# Revit family: Plate_System_Water_Coolers-Zurn-Industries-Z1224
name_source: partatom
category: Plumbing Fixtures
units: mm (PartAtom-declared; Revit-internal decimal feet)

## family parameters
Cut with Voids When Loaded = No
Host = Face
Maintain Annotation Orientation = No
OmniClass Number = 23.45.05.21.11.14
OmniClass Title = Chemical/Biological Sanitary Disposal Units
Part Type = Normal
Room Calculation Point = No
Round Connector Dimension = Use Diameter
Shared = No

## types (38) — shared parameters
A Dimension = 18.25 "
Approx.wt.lbs = 28
Assembly Code = D2030100
CW Connection = No
Curve inner radius = 1.5 "
Default Elevation = 25 "
Description = Plate Type System Lavatory With Back
HW Connection = No
Hardware = Steel - Zurn - Zinc Coated
Manufacturer = Zurn Water, LLC
Manufacturer Brand = Zurn
Model = Z1224
Modified Date = 10/31/2025
Product Data URL = https://www.bimobject.com
Product Documentation Link = https://files.zurn.com
Product Installation Sheet URL = https://files.zurn.com
Product Page URL = https://www.zurn.com
System with Universal Plate = Iron - Zurn - Cast - Painted - Blue
URL = www.zurn.com
Vent Connection = No
WFU = 1
Waste Connection = Yes
Width = 2.5 "
zero-valued in all types: CWFU, HWFU

## per-type parameters (varying)
| type | B Dimension | D Dimension | D' Dimension (Zurn) | Double Installtion Holes | E Dimension | E' Dimension | H Dimension | Single Installation Holes | Type Comments |
| American Standard®-Allbrook™ (6541.132) | 31.75 " | 12 " | 1.188 " | No | 0.594 " | 0.594 " | 36 " | Yes | American Standard®-Allbrook™ (6541.132) |
| Zurn-Small Waterless (Z5796) | 30.875 " | 12 " | 1 " | No | 0.5 " | 0.5 " | 36 " | Yes | Zurn-Small Waterless (Z5796) |
| Zurn-Urinal (Z5740) | 31.75 " | 12 " | 1 " | No | 0.5 " | 0.5 " | 36 " | Yes | Zurn-Urinal (Z5740) |
| Zurn-Small Pint (Z5738) | 32 " | 12 " | 1 " | No | 0.5 " | 0.5 " | 36 " | Yes | Zurn-Small Pint (Z5738) |
| Kohler®-Bardon™ (K-4960) | 41.25 " | 12 " | 1 " | Yes | 0.5 " | 0.5 " | 48 " | No | Kohler®-Bardon™ (K-4960) |
| Kohler®-Bardon™ (K-4904-ET) | 41.25 " | 12 " | 1 " | Yes | 0.5 " | 0.5 " | 48 " | No | Kohler®-Bardon™ (K-4904-ET) |
| American Standard®-Trimbrook™ (6561-017) | 38.375 " | 11 " | 1 " | Yes | 0.594 " | 0.5 " | 42 " | No | American Standard®-Trimbrook™ (6561.017) |
| American Standard®-Washbrook™ (6590-525) | 39.5 " | 13.5 " | 1 " | Yes | 0.594 " | 0.5 " | 42 " | No | American Standard®-Washbrook™ (6590.525) |
| American Standard®-Washbrook™ (6590-125) | 39.5 " | 13.5 " | 1 " | Yes | 0.594 " | 0.5 " | 42 " | No | American Standard®-Washbrook™ (6590.125) |
| American Standard®-Washbrook™ (6515-125) | 39.5 " | 13.5 " | 1 " | Yes | 0.594 " | 0.5 " | 42 " | No | American Standard®-Washbrook™ (6515.125) |
| American Standard®-Washbrook™ (6506-011) | 39.75 " | 13.5 " | 1 " | Yes | 0.594 " | 0.5 " | 42 " | No | American Standard®-Washbrook™ (6506.011) |
| American Standard®-Washbrook™ (6501-010) | 39.75 " | 13.5 " | 1 " | Yes | 0.594 " | 0.5 " | 42 " | No | American Standard®-Washbrook™ (6501.010) |
| Eljer®-Signature™ (161-2095) | 36.5 " | 11 " | 1 " | Yes | 0.5 " | 0.5 " | 42 " | No | Eljer®-Signature™ (161-2095) |
| Eljer®-Signature™ (161-2090) | 36.5 " | 11 " | 1 " | Yes | 0.5 " | 0.5 " | 42 " | No | Eljer®-Signature™ (161-2090) |
| Eljer®-Bedfordshire™ (161-1190) | 32.125 " | 6 " | 1 " | Yes | 0.5 " | 0.5 " | 36 " | No | Eljer®-Bedfordshire™ (161-1190) |
| Eljer®-Dover™ (161-1150) | 33.125 " | 6 " | 1 " | Yes | 0.5 " | 0.5 " | 36 " | No | Eljer®-Dover™ (161-1150) |
| Eljer®-Savon™ (161-1095) | 36.5 " | 11 " | 1 " | Yes | 0.5 " | 0.5 " | 42 " | No | Eljer®-Savon™ (161-1095) |
| Eljer®-Savon™ (161-1090) | 36.5 " | 11 " | 1 " | Yes | 0.5 " | 0.5 " | 42 " | No | Eljer®-Savon™ (161-1090) |
| Eljer®-Correcto™ (161-1075) | 40.125 " | 12 " | 1 " | Yes | 0.5 " | 0.5 " | 48 " | No | Eljer®-Correcto™ (161-1075) |
| Eljer®-Correcto™ (161-1060) | 40.125 " | 12 " | 1 " | Yes | 0.5 " | 0.5 " | 48 " | No | Eljer®-Correcto™ (161-1060) |
| Eljer®-Correcto™ (161-1045) | 40.125 " | 12 " | 1 " | Yes | 0.5 " | 0.5 " | 48 " | No | Eljer®-Correcto™ (161-1045) |
| Zurn-Urinal (Z5730) | 31.75 " | 12 " | 1 " | No | 0.5 " | 0.5 " | 36 " | Yes | Zurn-Urinal (Z5730) |
| Eljer®-Correcto™ (161-1030) | 40.125 " | 12 " | 1 " | Yes | 0.5 " | 0.5 " | 48 " | No | Eljer®-Correcto™ (161-1030) |
| American Standard®-Pintbrook™ (6002-001) | 33.375 " | 6 " | 1 " | Yes | 0.594 " | 0.5 " | 36 " | No | American Standard®-Pintbrook™ (6002.001) |
| Eljer®-Correcto™ (161-1035) | 40.125 " | 12 " | 1 " | Yes | 0.5 " | 0.5 " | 48 " | No | Eljer®-Correcto™ (161-1035) |
| Eljer®-Correcto™ (161-1050) | 40.125 " | 12 " | 1 " | Yes | 0.5 " | 0.5 " | 48 " | No | Eljer®-Correcto™ (161-1050) |
| Eljer®-Correcto™ (161-1065) | 40.125 " | 12 " | 1 " | Yes | 0.5 " | 0.5 " | 48 " | No | Eljer®-Correcto™ (161-1065) |
| Eljer®-Correcto™ (161-1080) | 40.125 " | 12 " | 1 " | Yes | 0.5 " | 0.5 " | 48 " | No | Eljer®-Correcto™ (161-1080) |
| Eljer®-Correcto™ (161-2030) | 40.125 " | 12 " | 1 " | Yes | 0.5 " | 0.5 " | 48 " | No | Eljer®-Correcto™ (161-2030) |
| Eljer®-Terminal™ (161-1100) | 34.625 " | 9.5 " | 1 " | Yes | 0.5 " | 0.5 " | 42 " | No | Eljer®-Terminal™ (161-1100) |
| Eljer®-Dover™ (161-1155) | 33.125 " | 6 " | 1 " | Yes | 0.5 " | 0.5 " | 36 " | No | Eljer®-Dover™ (161-1155) |
| Zurn-Urinal (Z5750) | 38.75 " | 14 " | 1 " | Yes | 0.5 " | 0.5 " | 42 " | No | Zurn-Urinal (Z5750) |
| Zurn-Retro Pint (Z5758) | 41.125 " | 14 " | 1 " | Yes | 0.5 " | 0.5 " | 48 " | No | Zurn-Retro Pint (Z5758) |
| Zurn-Retro Pint (Z5759) | 41.125 " | 14 " | 1 " | Yes | 0.5 " | 0.5 " | 48 " | No | Zurn-Retro Pint (Z5759) |
| Zurn-Urinal (Z5760) | 38.75 " | 14 " | 1 " | Yes | 0.5 " | 0.5 " | 42 " | No | Zurn-Urinal (Z5760) |
| Zurn-Waterless (Z5795) | 39.75 " | 14 " | 1 " | Yes | 0.5 " | 0.5 " | 42 " | No | Zurn-Waterless (Z5795) |
| Zurn-"The Pint" (Z5798) | 38.75 " | 14 " | 1 " | Yes | 0.5 " | 0.5 " | 42 " | No | Zurn-""The Pint"" (Z5798) |
| Zurn-"The Pint" (Z5799) | 38.75 " | 14 " | 1 " | Yes | 0.5 " | 0.5 " | 42 " | No | Zurn-""The Pint"" (Z5799) |

## geometry (parser evidence)
native form markers: Blend x4, Sweep x3
no freeform markers — native parametric forms only
